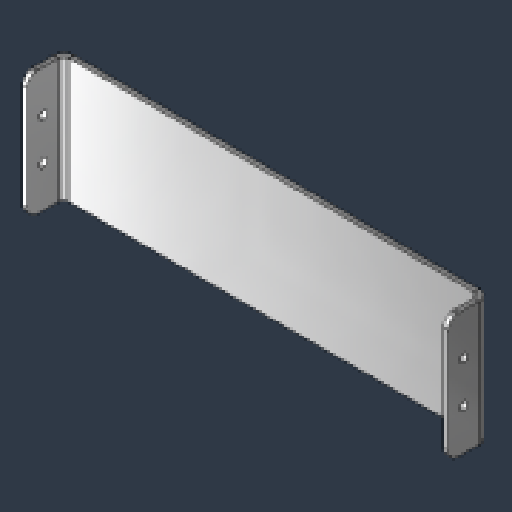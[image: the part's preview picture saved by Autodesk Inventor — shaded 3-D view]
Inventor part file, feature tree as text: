
AUTODESK INVENTOR PART (.ipt)
format: ipt  version: 2024.3 (Build 283343000, 343)  size: 214,528 bytes
history: native  units: in
note: dims shown in document units (in); Inventor stores cm internally (conversion verified against a paired STEP export)
features: sheet_metal_op x4, sketch x4, chamfer x2, other x2, hole x1, extrude x1, projected_geometry x1
ambient origin geometry x8: Origin, YZ Plane, XZ Plane, XY Plane, X Axis, Y Axis, Z Axis, Center Point
bodies: Solid1 (feature_tree)
feature tree (15):
  sheet_metal_op  "Face1"
  sheet_metal_op  "Flange1"
  hole  "Hole1"  [1 undecoded]
  chamfer  "Corner Round1"
  extrude  "Extrusion2"  Depth=0.125in
  chamfer  "Corner Round2"
  sketch  "Sketch1"  dims[d0=10.27in d1=3.0in]
  other  "Plate1"
  sketch  "Sketch2"  dims[d2=0.125in d3=0.125in]
  other  "Plate2"
  sheet_metal_op  "Bend1"
  sheet_metal_op  "Corner1"
  sketch  "Sketch3"  dims[d4=0.0625in]
  sketch  "Sketch5"  dims[d5=0.25in d6=0.125in d7=1.0in d8=90.0deg d9=0.125in d10=0.5in d11=0.125in d12=0.125in d13=1.0in d14=0.375in d15=0.201in d16=0.75in d17=0.385in d18=0.25in d19=0.5635in d20=0.125in d21=0.8108in d39=0.25in d40=0.5in d41=0.5in d43=0.5in d44=0.125in d45=0.0in d46=0.125in]
  projected_geometry  "Projected Loop1"
note: 1 required parameter value undecoded (feature->parameter linkage not recoverable at this tier; creation-order binding heuristic only, values carry confidence <= 0.55)
